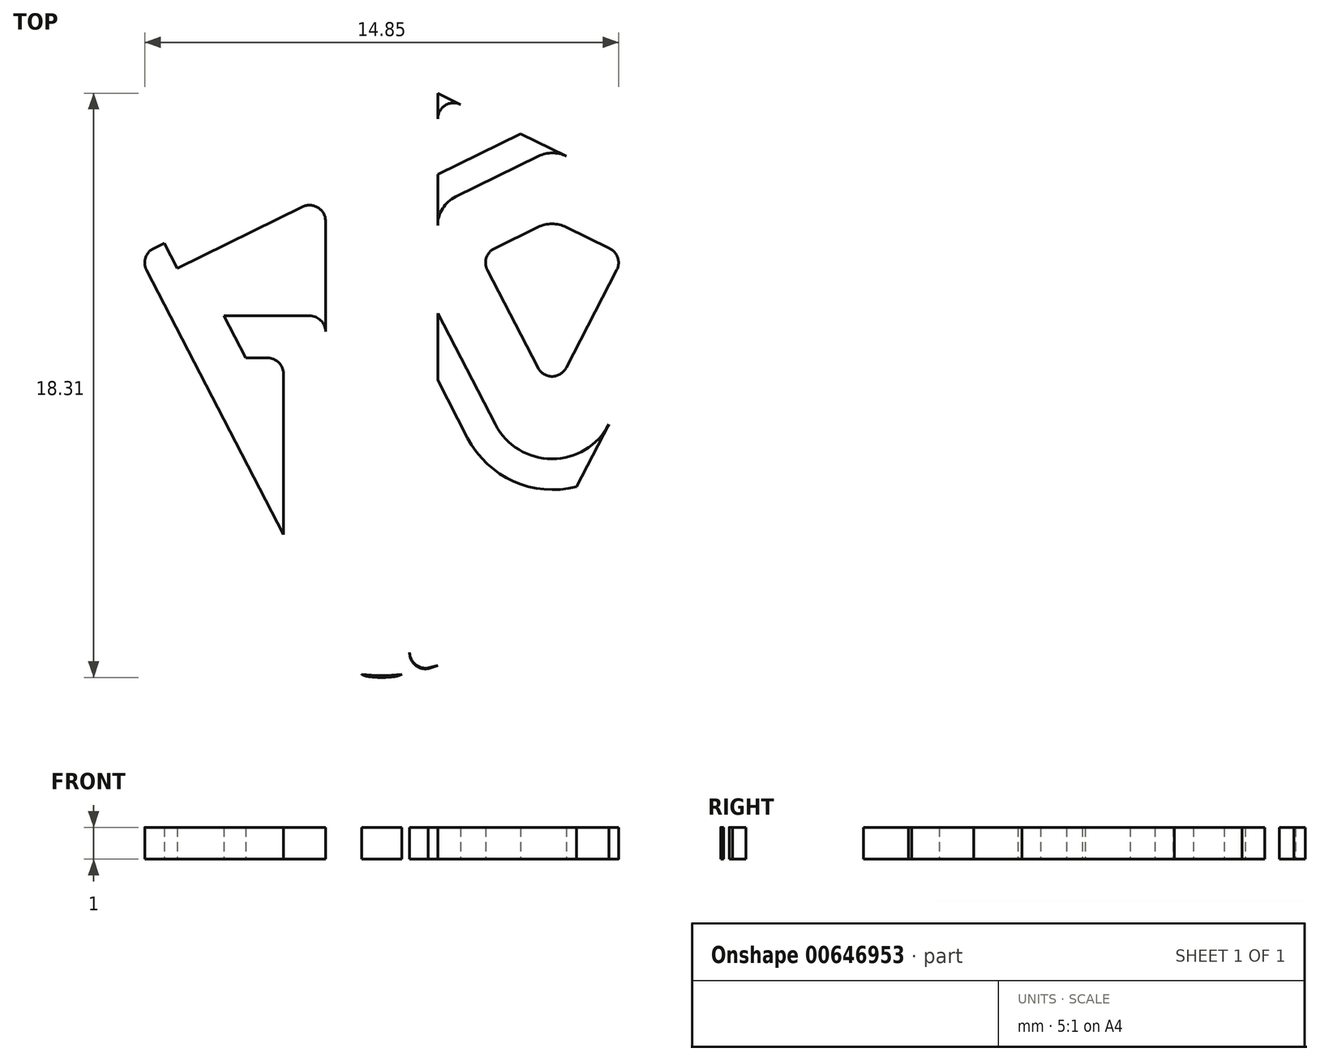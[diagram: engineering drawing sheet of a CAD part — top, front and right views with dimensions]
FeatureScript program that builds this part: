
annotation { "Feature Type Name" : "Feature", "Feature Type Description" : "" }
export const myFeature = defineFeature(function(context is Context, id is Id, definition is map)
    precondition{}
    {
        {
            var Q0;
            Q0=qCreatedBy(makeId("Top.planeOp"),FACE);
            var sketch = newSketch(context, id + "F0", { "sketchPlane" : qUnion([Q0])});
            skArc(sketch, "E0.MirrorCS", {"start": v(-12.62, 8.93) * mm, "mid": v(-12.18, 9.03) * mm, "end": v(-11.74, 8.93) * mm});
            skArc(sketch, "E1.MirrorCS", {"start": v(-1.42, 3.88) * mm, "mid": v(-0.9, 3.3) * mm, "end": v(-0.97, 2.52) * mm});
            skArc(sketch, "E2.MirrorCS", {"start": v(-23.38, 2.52) * mm, "mid": v(-23.45, 3.3) * mm, "end": v(-22.94, 3.88) * mm});
            skPoint(sketch, "E3.MirrorP", {"position": v(-23.85, 3.43) * mm});
            skArc(sketch, "E4.MirrorCS", {"start": v(-6.85, -8.84) * mm, "mid": v(-12.18, -12.09) * mm, "end": v(-17.5, -8.84) * mm});
            skLineSegment(sketch, "E5.MirrorCS", {"start": v(-4.15, -3.64) * mm, "end": v(-0.97, 2.52) * mm});
            skLineSegment(sketch, "E6.MirrorCS", {"start": v(-12.62, 8.93) * mm, "end": v(-22.94, 3.88) * mm});
            skLineSegment(sketch, "E7.MirrorCS", {"start": v(-23.38, 2.52) * mm, "end": v(-17.5, -8.84) * mm});
            skLineSegment(sketch, "E8.MirrorCS", {"start": v(-1.42, 3.88) * mm, "end": v(-11.74, 8.93) * mm});
            skLineSegment(sketch, "E9", {"start": v(-22.26, 2.53) * mm, "end": v(-16.62, -8.38) * mm});
            skArc(sketch, "E10.filletArc", {"start": v(-9.67, -10.41) * mm, "mid": v(-8.56, -9.53) * mm, "end": v(-7.74, -8.38) * mm});
            skLineSegment(sketch, "E11.MirrorCS", {"start": v(-10.42, 3.03) * mm, "end": v(-10.42, 0.52) * mm});
            skLineSegment(sketch, "E12.bottom", {"start": v(-15.25, 0.2) * mm, "end": v(-16.07, 0.2) * mm});
            skLineSegment(sketch, "E12.top", {"start": v(-15.75, -1.12) * mm, "end": v(-16.07, -1.12) * mm});
            skLineSegment(sketch, "E13", {"start": v(-15.25, 0.2) * mm, "end": v(-14.44, 0.2) * mm});
            skPoint(sketch, "E14", {"position": v(-16.57, -8.47) * mm});
            skPoint(sketch, "E15", {"position": v(-15.25, -10.03) * mm});
            skPoint(sketch, "E16", {"position": v(-13.94, -10.77) * mm});
            skPoint(sketch, "E17", {"position": v(-13.06, -11) * mm});
            skPoint(sketch, "E18", {"position": v(-11.3, -11) * mm});
            skPoint(sketch, "E19", {"position": v(-10.42, -10.77) * mm});
            skPoint(sketch, "E20", {"position": v(-9.1, -10.03) * mm});
            skPoint(sketch, "E21", {"position": v(-9.1, -6.67) * mm});
            skPoint(sketch, "E22", {"position": v(-2.78, 1.2) * mm});
            skPoint(sketch, "E23", {"position": v(-4.57, 2.08) * mm});
            skPoint(sketch, "E24", {"position": v(-9.1, 6.52) * mm});
            skPoint(sketch, "E25", {"position": v(-10.42, 7.17) * mm});
            skPoint(sketch, "E26", {"position": v(-11.3, 7.6) * mm});
            skPoint(sketch, "E27", {"position": v(-13.06, 7.6) * mm});
            skPoint(sketch, "E28", {"position": v(-13.94, 7.17) * mm});
            skPoint(sketch, "E29", {"position": v(-15.25, 4.3) * mm});
            skPoint(sketch, "E30", {"position": v(-13.94, 4.94) * mm});
            skPoint(sketch, "E31", {"position": v(-13.06, 5.37) * mm});
            skPoint(sketch, "E32", {"position": v(-10.42, 4.94) * mm});
            skPoint(sketch, "E33", {"position": v(-21.58, 1.2) * mm});
            skPoint(sketch, "E34", {"position": v(-19.78, 2.08) * mm});
            skPoint(sketch, "E35", {"position": v(-16.57, -4.12) * mm});
            skPoint(sketch, "E36", {"position": v(-16.57, -1.12) * mm});
            skPoint(sketch, "E37", {"position": v(-16.57, 0.2) * mm});
            skPoint(sketch, "E38", {"position": v(-15.25, 0.2) * mm});
            skPoint(sketch, "E39", {"position": v(-15.25, -1.12) * mm});
            skPoint(sketch, "E40", {"position": v(-13.94, 0.2) * mm});
            skLineSegment(sketch, "E41", {"start": v(-2.78, 1.2) * mm, "end": v(-2.1, 2.53) * mm});
            skLineSegment(sketch, "E42", {"start": v(-3.82, 3.94) * mm, "end": v(-6.39, 5.2) * mm});
            skLineSegment(sketch, "E43", {"start": v(-6.4, -1.43) * mm, "end": v(-4.8, 1.63) * mm});
            skLineSegment(sketch, "E44", {"start": v(-5.03, 2.3) * mm, "end": v(-6.4, 2.97) * mm});
            skLineSegment(sketch, "E45", {"start": v(-9.1, 3.5) * mm, "end": v(-9.1, -6.67) * mm});
            skLineSegment(sketch, "E46", {"start": v(-22.04, 3.2) * mm, "end": v(-14.65, 6.82) * mm});
            skLineSegment(sketch, "E47", {"start": v(-12.78, 7.74) * mm, "end": v(-12.4, 7.92) * mm});
            skLineSegment(sketch, "E48", {"start": v(-11.96, 7.92) * mm, "end": v(-11.58, 7.74) * mm});
            skLineSegment(sketch, "E49", {"start": v(-15.25, 4.3) * mm, "end": v(-19.32, 2.3) * mm});
            skLineSegment(sketch, "E50", {"start": v(-19.55, 1.63) * mm, "end": v(-16.57, -4.12) * mm});
            skLineSegment(sketch, "E51", {"start": v(-15.25, -1.62) * mm, "end": v(-15.25, -10.03) * mm});
            skPoint(sketch, "E52", {"position": v(-15.25, -6.67) * mm});
            skLineSegment(sketch, "E53", {"start": v(-16.57, -4.12) * mm, "end": v(-15.25, -6.67) * mm});
            skLineSegment(sketch, "E54", {"start": v(-15.25, 4.3) * mm, "end": v(-14.65, 4.59) * mm});
            skLineSegment(sketch, "E55", {"start": v(-9.1, 6.52) * mm, "end": v(-9.7, 6.82) * mm});
            skArc(sketch, "E56.filletArc", {"start": v(-22.04, 3.2) * mm, "mid": v(-22.3, 2.91) * mm, "end": v(-22.26, 2.53) * mm});
            skArc(sketch, "E57.filletArc", {"start": v(-2.1, 2.53) * mm, "mid": v(-2.06, 2.91) * mm, "end": v(-2.32, 3.2) * mm});
            skArc(sketch, "E58.filletArc", {"start": v(-13.94, 6.37) * mm, "mid": v(-14.17, 6.8) * mm, "end": v(-14.65, 6.82) * mm});
            skArc(sketch, "E59.filletArc", {"start": v(-9.7, 6.82) * mm, "mid": v(-10.18, 6.8) * mm, "end": v(-10.42, 6.37) * mm});
            skArc(sketch, "E60.filletArc", {"start": v(-8.38, 3.94) * mm, "mid": v(-8.87, 3.92) * mm, "end": v(-9.1, 3.5) * mm});
            skArc(sketch, "E61.filletArc", {"start": v(-4.8, 1.63) * mm, "mid": v(-4.78, 2.01) * mm, "end": v(-5.03, 2.3) * mm});
            skArc(sketch, "E62.filletArc", {"start": v(-19.32, 2.3) * mm, "mid": v(-19.58, 2.01) * mm, "end": v(-19.55, 1.63) * mm});
            skArc(sketch, "E63.filletArc", {"start": v(-13.94, 4.14) * mm, "mid": v(-14.17, 4.56) * mm, "end": v(-14.65, 4.59) * mm});
            skArc(sketch, "E64.filletArc", {"start": v(-15.25, -1.62) * mm, "mid": v(-15.4, -1.27) * mm, "end": v(-15.75, -1.12) * mm});
            skArc(sketch, "E65.filletArc", {"start": v(-13.94, -0.3) * mm, "mid": v(-14.08, 0.05) * mm, "end": v(-14.44, 0.2) * mm});
            skLineSegment(sketch, "E66", {"start": v(-13.94, 4.14) * mm, "end": v(-13.94, 6.37) * mm});
            skArc(sketch, "E67.filletArc", {"start": v(-11.96, 7.92) * mm, "mid": v(-12.18, 7.97) * mm, "end": v(-12.4, 7.92) * mm});
            skArc(sketch, "E68.filletArc", {"start": v(-12.78, 7.74) * mm, "mid": v(-12.98, 7.55) * mm, "end": v(-13.06, 7.29) * mm});
            skArc(sketch, "E69.filletArc", {"start": v(-11.3, 7.29) * mm, "mid": v(-11.37, 7.55) * mm, "end": v(-11.58, 7.74) * mm});
            skArc(sketch, "E70.filletArc", {"start": v(-10.42, -9.98) * mm, "mid": v(-10.17, -10.41) * mm, "end": v(-9.67, -10.41) * mm});
            skArc(sketch, "E71.MirrorCS", {"start": v(-14.69, -10.41) * mm, "mid": v(-15.8, -9.53) * mm, "end": v(-16.62, -8.38) * mm});
            skArc(sketch, "E72.MirrorCS", {"start": v(-13.94, -9.98) * mm, "mid": v(-14.19, -10.41) * mm, "end": v(-14.69, -10.41) * mm});
            skArc(sketch, "E73", {"start": v(-12.63, -11.1) * mm, "mid": v(-12.18, -11.14) * mm, "end": v(-11.72, -11.1) * mm});
            skLineSegment(sketch, "E74", {"start": v(-13.94, -9.98) * mm, "end": v(-13.94, -0.3) * mm});
            skLineSegment(sketch, "E75", {"start": v(-13.06, -10.37) * mm, "end": v(-13.06, 6.8) * mm});
            skLineSegment(sketch, "E76", {"start": v(-11.3, 7.29) * mm, "end": v(-11.3, -10.35) * mm});
            skArc(sketch, "E77.filletArc", {"start": v(-13.06, -10.61) * mm, "mid": v(-12.94, -10.94) * mm, "end": v(-12.63, -11.1) * mm});
            skArc(sketch, "E78.filletArc", {"start": v(-11.72, -11.1) * mm, "mid": v(-11.42, -10.94) * mm, "end": v(-11.3, -10.61) * mm});
            skLineSegment(sketch, "E79", {"start": v(-16.07, 0.2) * mm, "end": v(-17.12, 0.2) * mm});
            skLineSegment(sketch, "E80", {"start": v(-16.07, -1.12) * mm, "end": v(-16.57, -1.12) * mm});
            skPoint(sketch, "E81", {"position": v(-16.43, -1.12) * mm});
            skLineSegment(sketch, "E82", {"start": v(-16.43, -1.12) * mm, "end": v(-17.12, 0.2) * mm});
            skPoint(sketch, "E83", {"position": v(-6.84, 2.08) * mm});
            skPoint(sketch, "E84", {"position": v(-6.84, 3.19) * mm});
            skPoint(sketch, "E85", {"position": v(-6.84, -2.3) * mm});
            skPoint(sketch, "E86", {"position": v(-9.1, 2.08) * mm});
            skLineSegment(sketch, "E87", {"start": v(-7.28, 2.97) * mm, "end": v(-8.64, 2.3) * mm});
            skLineSegment(sketch, "E88", {"start": v(-8.87, 1.63) * mm, "end": v(-7.28, -1.43) * mm});
            skPoint(sketch, "E89", {"position": v(-6.83, 5.4) * mm});
            skPoint(sketch, "E90", {"position": v(-5.42, 0.45) * mm});
            skPoint(sketch, "E91", {"position": v(-10.42, 3.65) * mm});
            skLineSegment(sketch, "E92", {"start": v(-9.86, 3.93) * mm, "end": v(-7.27, 5.2) * mm});
            skPoint(sketch, "E93", {"position": v(-7.96, -4.47) * mm});
            skPoint(sketch, "E94", {"position": v(-10.42, 0.28) * mm});
            skPoint(sketch, "E95", {"position": v(-9.1, -2.27) * mm});
            skLineSegment(sketch, "E96", {"start": v(-6.84, 3.19) * mm, "end": v(-6.84, 2.08) * mm});
            skPoint(sketch, "E97", {"position": v(-3.26, 0.28) * mm});
            skPoint(sketch, "E98", {"position": v(-3.26, 3.66) * mm});
            skLineSegment(sketch, "E99", {"start": v(-3.26, 3.04) * mm, "end": v(-3.26, 0.52) * mm});
            skLineSegment(sketch, "E100", {"start": v(-12.18, -6.09) * mm, "end": v(-12.18, -8.2) * mm});
            skLineSegment(sketch, "E101.MirrorCS", {"start": v(-21.1, 3.66) * mm, "end": v(-21.1, 0.28) * mm});
            skLineSegment(sketch, "E102.MirrorCS", {"start": v(-4.57, 2.08) * mm, "end": v(-6.84, -2.3) * mm});
            skLineSegment(sketch, "E103.MirrorCS", {"start": v(-6.84, 3.19) * mm, "end": v(-4.57, 2.08) * mm});
            skPoint(sketch, "E104", {"position": v(-11.3, 5.38) * mm});
            skPoint(sketch, "E105", {"position": v(-11.3, -10.04) * mm});
            skPoint(sketch, "E106", {"position": v(-13.06, -10.04) * mm});
            skPoint(sketch, "E107", {"position": v(-12.17, 5.8) * mm});
            skPoint(sketch, "E108", {"position": v(-13.06, -6.65) * mm});
            skPoint(sketch, "E109", {"position": v(-11.3, -6.65) * mm});
            skLineSegment(sketch, "E110", {"start": v(-13.94, 7.17) * mm, "end": v(-13.78, 7.25) * mm});
            skLineSegment(sketch, "E111", {"start": v(-13.06, 5.37) * mm, "end": v(-13.06, 7.6) * mm});
            skArc(sketch, "E112.filletArc", {"start": v(-13.06, 6.8) * mm, "mid": v(-13.3, 7.22) * mm, "end": v(-13.78, 7.25) * mm});
            skLineSegment(sketch, "E113", {"start": v(-13.94, 7.17) * mm, "end": v(-12.78, 7.74) * mm});
            skLineSegment(sketch, "E114", {"start": v(-11.3, -10.04) * mm, "end": v(-11.3, -11) * mm});
            skLineSegment(sketch, "E115", {"start": v(-10.42, -10.77) * mm, "end": v(-10.67, -10.83) * mm});
            skArc(sketch, "E116.filletArc", {"start": v(-11.3, -10.35) * mm, "mid": v(-11.1, -10.75) * mm, "end": v(-10.67, -10.83) * mm});
            skLineSegment(sketch, "E117", {"start": v(-13.06, -10.04) * mm, "end": v(-13.06, -11) * mm});
            skLineSegment(sketch, "E118", {"start": v(-14.06, -10.77) * mm, "end": v(-13.67, -10.86) * mm});
            skPoint(sketch, "E119.newPointA", {"position": v(-13.06, -10.61) * mm});
            skArc(sketch, "E119.filletArc", {"start": v(-13.67, -10.86) * mm, "mid": v(-13.25, -10.77) * mm, "end": v(-13.06, -10.37) * mm});
            skLineSegment(sketch, "E120", {"start": v(-21.58, 1.2) * mm, "end": v(-16.62, -8.38) * mm});
            skPoint(sketch, "E121", {"position": v(-12.18, -16.97) * mm});
            skArc(sketch, "E122.filletArc", {"start": v(-16.62, -8.38) * mm, "mid": v(-12.18, -11.09) * mm, "end": v(-7.74, -8.38) * mm});
            skArc(sketch, "E123.filletArc", {"start": v(-6.39, 5.2) * mm, "mid": v(-6.83, 5.3) * mm, "end": v(-7.27, 5.2) * mm});
            skArc(sketch, "E124.filletArc", {"start": v(-3.26, 3.04) * mm, "mid": v(-3.4, 3.57) * mm, "end": v(-3.82, 3.94) * mm});
            skArc(sketch, "E125.filletArc", {"start": v(-3.37, 0.06) * mm, "mid": v(-3.28, 0.28) * mm, "end": v(-3.26, 0.52) * mm});
            skArc(sketch, "E126.filletArc", {"start": v(-9.86, 3.93) * mm, "mid": v(-10.27, 3.56) * mm, "end": v(-10.42, 3.03) * mm});
            skArc(sketch, "E127.filletArc", {"start": v(-10.42, 0.52) * mm, "mid": v(-10.4, 0.28) * mm, "end": v(-10.3, 0.06) * mm});
            skArc(sketch, "E128.filletArc", {"start": v(-6.4, 2.97) * mm, "mid": v(-6.84, 3.08) * mm, "end": v(-7.28, 2.97) * mm});
            skArc(sketch, "E129.filletArc", {"start": v(-8.64, 2.3) * mm, "mid": v(-8.9, 2.01) * mm, "end": v(-8.87, 1.63) * mm});
            skLineSegment(sketch, "E130", {"start": v(-3.82, 3.94) * mm, "end": v(-11.3, 7.6) * mm});
            skLineSegment(sketch, "E131", {"start": v(-10.42, 0.52) * mm, "end": v(-10.42, 7.17) * mm});
            skLineSegment(sketch, "E132", {"start": v(-9.77, 4.95) * mm, "end": v(-7.83, 5.9) * mm});
            skLineSegment(sketch, "E133", {"start": v(-7.83, 5.9) * mm, "end": v(-9.77, 4.95) * mm});
            skLineSegment(sketch, "E134", {"start": v(-9.77, 4.95) * mm, "end": v(-10.42, 4.63) * mm});
            skPoint(sketch, "E135", {"position": v(-8.5, -3.42) * mm});
            skLineSegment(sketch, "E136", {"start": v(-16.9, 2.51) * mm, "end": v(-19.8, 1.1) * mm});
            skLineSegment(sketch, "E137", {"start": v(-19.8, 1.1) * mm, "end": v(-16.9, 2.51) * mm});
            skLineSegment(sketch, "E138", {"start": v(-16.9, 2.51) * mm, "end": v(-14.65, 3.61) * mm});
            skLineSegment(sketch, "E139", {"start": v(-19.12, 0.8) * mm, "end": v(-18.34, 1.21) * mm});
            skLineSegment(sketch, "E140", {"start": v(-18.34, 1.21) * mm, "end": v(-19.55, 3.55) * mm});
            skLineSegment(sketch, "E141", {"start": v(-19.55, 3.55) * mm, "end": v(-18.34, 1.21) * mm});
            skLineSegment(sketch, "E142", {"start": v(-19.55, 3.55) * mm, "end": v(-15.64, -4.01) * mm});
            skLineSegment(sketch, "E143", {"start": v(-16.13, -2.63) * mm, "end": v(-16.13, -3.81) * mm});
            skLineSegment(sketch, "E144", {"start": v(-16.13, -1.46) * mm, "end": v(-16.13, -3.81) * mm});
            skLineSegment(sketch, "E145", {"start": v(-13.94, 3.16) * mm, "end": v(-13.94, -0.3) * mm});
            skLineSegment(sketch, "E146", {"start": v(-15.25, 1.07) * mm, "end": v(-18.6, 1.07) * mm});
            skLineSegment(sketch, "E147", {"start": v(-18.6, 1.07) * mm, "end": v(-15.25, 1.07) * mm});
            skLineSegment(sketch, "E148", {"start": v(-13.7, 1.07) * mm, "end": v(-15.25, 1.07) * mm});
            skArc(sketch, "E149.filletArc", {"start": v(-13.94, 3.16) * mm, "mid": v(-14.17, 3.59) * mm, "end": v(-14.65, 3.61) * mm});
            skLineSegment(sketch, "E150", {"start": v(-2.38, 2.4) * mm, "end": v(-2.38, 1.75) * mm});
            skLineSegment(sketch, "E151", {"start": v(-2.38, 1.75) * mm, "end": v(-2.38, 3.6) * mm});
            skLineSegment(sketch, "E152", {"start": v(-3.82, 3.94) * mm, "end": v(-1.86, 2.98) * mm});
            skLineSegment(sketch, "E153", {"start": v(-16.07, -2) * mm, "end": v(-17.03, -2) * mm});
            skArc(sketch, "E154.filletArc", {"start": v(-7.28, -1.43) * mm, "mid": v(-6.84, -1.7) * mm, "end": v(-6.4, -1.43) * mm});
            skLineSegment(sketch, "E155", {"start": v(-7.74, -8.38) * mm, "end": v(-6.84, -6.65) * mm});
            skPoint(sketch, "E156", {"position": v(-7.9, 1.68) * mm});
            skPoint(sketch, "E157", {"position": v(-6.86, 2.22) * mm});
            skPoint(sketch, "E158", {"position": v(-5.77, 1.69) * mm});
            skPoint(sketch, "E159", {"position": v(-6.84, -0.38) * mm});
            skLineSegment(sketch, "E160", {"start": v(-7.9, 1.68) * mm, "end": v(-6.86, 2.22) * mm});
            skLineSegment(sketch, "E161", {"start": v(-6.86, 2.22) * mm, "end": v(-5.77, 1.69) * mm});
            skLineSegment(sketch, "E162", {"start": v(-5.77, 1.69) * mm, "end": v(-6.84, -0.38) * mm});
            skLineSegment(sketch, "E163", {"start": v(-6.84, -0.38) * mm, "end": v(-7.9, 1.68) * mm});
            skLineSegment(sketch, "E164.MirrorCS", {"start": v(-10.42, -9.98) * mm, "end": v(-10.42, -0.3) * mm});
            skPoint(sketch, "E165", {"position": v(-6.82, -8.79) * mm});
            skLineSegment(sketch, "E166", {"start": v(-6.85, -8.84) * mm, "end": v(-6.82, -8.79) * mm});
            skPoint(sketch, "E167", {"position": v(-6.84, -6.65) * mm});
            skLineSegment(sketch, "E168", {"start": v(-2.78, 1.2) * mm, "end": v(-5.06, -3.21) * mm});
            skLineSegment(sketch, "E169", {"start": v(-8.61, -3.21) * mm, "end": v(-10.42, 0.28) * mm});
            skLineSegment(sketch, "E170", {"start": v(-10.42, 0.52) * mm, "end": v(-10.42, -0.3) * mm});
            skArc(sketch, "E171.filletArc", {"start": v(-8.61, -3.21) * mm, "mid": v(-6.84, -4.3) * mm, "end": v(-5.06, -3.21) * mm});
            skPoint(sketch, "E172", {"position": v(-10.42, -1.83) * mm});
            skPoint(sketch, "E173", {"position": v(-9.1, -4.38) * mm});
            skLineSegment(sketch, "E174", {"start": v(-5.5, -4.07) * mm, "end": v(-5.06, -3.21) * mm});
            skLineSegment(sketch, "E175", {"start": v(-9.1, -2.27) * mm, "end": v(-8.17, -4.07) * mm});
            skPoint(sketch, "E176", {"position": v(-0.97, 2.52) * mm});
            skPoint(sketch, "E177", {"position": v(-4.15, -3.64) * mm});
            skLineSegment(sketch, "E178", {"start": v(-10.42, -1.83) * mm, "end": v(-9.48, -3.64) * mm});
            skArc(sketch, "E179.filletArc", {"start": v(-9.48, -3.64) * mm, "mid": v(-6.82, -5.26) * mm, "end": v(-4.15, -3.64) * mm});
            skLineSegment(sketch, "E180", {"start": v(-6.82, -8.79) * mm, "end": v(-4.15, -3.64) * mm});
            skLineSegment(sketch, "E181", {"start": v(-6.84, -6.65) * mm, "end": v(-3.26, 0.28) * mm});
            skArc(sketch, "E182.MirrorCS", {"start": v(-10.68, -10.86) * mm, "mid": v(-11.1, -10.77) * mm, "end": v(-11.3, -10.37) * mm});
            skArc(sketch, "E183.MirrorCS", {"start": v(-11.3, -10.61) * mm, "mid": v(-11.42, -10.94) * mm, "end": v(-11.72, -11.1) * mm});
            skArc(sketch, "E184.MirrorCS", {"start": v(-7.74, -8.38) * mm, "mid": v(-12.18, -11.09) * mm, "end": v(-16.62, -8.38) * mm});
            skSolve(sketch);
        }
        {
            var Q0;
            {var subQ4=sQuery(id+"F0.wireOp",EDGE,"E138");Q0=makeQuery(id+"F0.imprint","IMPRINT",FACE,{"disambiguationData":[TD([[makeQuery(id+"F0.imprint","IMPRINT",EDGE,{"derivedFrom":subQ4}),-1.0]])]});}
            var Q1;
            Q1=makeQuery(id+"F0.imprint","IMPRINT",FACE,{"disambiguationData":[TD([[makeQuery(id+"F0.imprint","IMPRINT",EDGE,{"derivedFrom":sQuery(id+"F0.wireOp",EDGE,"E12.bottom")}),-1.0]])]});
            var Q2;
            {var subQ0=sQuery(id+"F0.wireOp",EDGE,"E144");var subQ5=makeQuery(id+"F0.imprint","IMPRINT",VERTEX,{"derivedFrom":subQ0});Q2=makeQuery(id+"F0.imprint","IMPRINT",FACE,{"disambiguationData":[TD([[makeQuery(id+"F0.imprint","IMPRINT",EDGE,{"disambiguationData":[TD([[subQ5,1.0]])],"derivedFrom":subQ0}),-1.0]])]});}
            var Q3;
            {var subQ0=sQuery(id+"F0.wireOp",EDGE,"E62.filletArc");Q3=makeQuery(id+"F0.imprint","IMPRINT",FACE,{"disambiguationData":[TD([[makeQuery(id+"F0.imprint","IMPRINT",EDGE,{"derivedFrom":subQ0}),1.0]])]});}
            var Q4;
            {var subQ1=sQuery(id+"F0.wireOp",EDGE,"E139");var subQ4=sQuery(id+"F0.wireOp",EDGE,"E50");var subQ5=makeQuery(id+"F0.imprint","INTERSECT",VERTEX,{"derivedFrom":[subQ4,subQ1]});Q4=makeQuery(id+"F0.imprint","IMPRINT",FACE,{"disambiguationData":[TD([[makeQuery(id+"F0.imprint","IMPRINT",EDGE,{"disambiguationData":[TD([[subQ5,1.0]])],"derivedFrom":subQ4}),1.0]])]});}
            var Q5;
            {var subQ0=sQuery(id+"F0.wireOp",EDGE,"E142");var subQ1=sQuery(id+"F0.wireOp",EDGE,"E139");var subQ2=makeQuery(id+"F0.imprint","INTERSECT",VERTEX,{"derivedFrom":[subQ1,subQ0]});Q5=makeQuery(id+"F0.imprint","IMPRINT",FACE,{"disambiguationData":[TD([[makeQuery(id+"F0.imprint","IMPRINT",EDGE,{"disambiguationData":[TD([[subQ2,1.0]])],"derivedFrom":subQ1}),-1.0]])]});}
            var Q6;
            {var subQ0=sQuery(id+"F0.wireOp",EDGE,"ozTpNQaU-grU3-HA9w-UyX2-o1CqBorec6r5");Q6=makeQuery(id+"F0.imprint","IMPRINT",FACE,{"disambiguationData":[TD([[makeQuery(id+"F0.imprint","IMPRINT",EDGE,{"derivedFrom":subQ0}),-1.0]])]});}
            var Q7;
            {var subQ2=sQuery(id+"F0.wireOp",EDGE,"3e2ccfe4-6b2a-43d4-8b51-7597902346a8.filletArc");Q7=makeQuery(id+"F0.imprint","IMPRINT",FACE,{"disambiguationData":[TD([[makeQuery(id+"F0.imprint","IMPRINT",EDGE,{"derivedFrom":subQ2}),-1.0]])]});}
            var Q8;
            Q8=makeQuery(id+"F0.imprint","IMPRINT",FACE,{"disambiguationData":[TD([[makeQuery(id+"F0.imprint","IMPRINT",EDGE,{"derivedFrom":sQuery(id+"F0.wireOp",EDGE,"E92")}),1.0]])]});
            var Q9;
            {var subQ3=sQuery(id+"F0.wireOp",EDGE,"E160");Q9=makeQuery(id+"F0.imprint","IMPRINT",FACE,{"disambiguationData":[TD([[makeQuery(id+"F0.imprint","IMPRINT",EDGE,{"derivedFrom":subQ3}),-1.0]])]});}
            var Q10;
            {var subQ7=sQuery(id+"F0.wireOp",EDGE,"E61.filletArc");Q10=makeQuery(id+"F0.imprint","IMPRINT",FACE,{"disambiguationData":[TD([[makeQuery(id+"F0.imprint","IMPRINT",EDGE,{"derivedFrom":subQ7}),1.0]])]});}
            var Q11;
            {var subQ5=sQuery(id+"F0.wireOp",EDGE,"E171.filletArc");Q11=makeQuery(id+"F0.imprint","IMPRINT",FACE,{"disambiguationData":[TD([[makeQuery(id+"F0.imprint","IMPRINT",EDGE,{"derivedFrom":subQ5}),-1.0]])]});}
            var Q12;
            {var subQ8=sQuery(id+"F0.wireOp",EDGE,"Ewz0VHGi-sKfj-zBBT-7Waf-a84nxzi6t6Pn");Q12=makeQuery(id+"F0.imprint","IMPRINT",FACE,{"disambiguationData":[TD([[makeQuery(id+"F0.imprint","IMPRINT",EDGE,{"derivedFrom":subQ8}),1.0]])]});}
            var Q13;
            {var subQ8=sQuery(id+"F0.wireOp",EDGE,"E178");Q13=makeQuery(id+"F0.imprint","IMPRINT",FACE,{"disambiguationData":[TD([[makeQuery(id+"F0.imprint","IMPRINT",EDGE,{"derivedFrom":subQ8}),1.0]])]});}
            var Q14;
            {var subQ0=sQuery(id+"F0.wireOp",EDGE,"E59.filletArc");Q14=makeQuery(id+"F0.imprint","IMPRINT",FACE,{"disambiguationData":[TD([[makeQuery(id+"F0.imprint","IMPRINT",EDGE,{"derivedFrom":subQ0}),-1.0]])]});}
            var Q15;
            {var subQ2=sQuery(id+"F0.wireOp",EDGE,"E115");Q15=makeQuery(id+"F0.imprint","IMPRINT",FACE,{"disambiguationData":[TD([[makeQuery(id+"F0.imprint","IMPRINT",EDGE,{"derivedFrom":subQ2}),1.0]])]});}
            var Q16;
            {var subQ0=sQuery(id+"F0.wireOp",EDGE,"E73");Q16=makeQuery(id+"F0.imprint","IMPRINT",FACE,{"disambiguationData":[TD([[makeQuery(id+"F0.imprint","IMPRINT",EDGE,{"derivedFrom":subQ0}),1.0]])]});}
            var Q17;
            Q17=makeQuery(id+"F0.imprint","IMPRINT",FACE,{"disambiguationData":[TD([[makeQuery(id+"F0.imprint","IMPRINT",EDGE,{"derivedFrom":sQuery(id+"F0.wireOp",EDGE,"E0.MirrorCS")}),-1.0]])]});
            extrude(context, id + "F1", {"entities" : qUnion([Q0, Q1, Q2, Q3, Q4, Q5, Q6, Q7, Q8, Q9, Q10, Q11, Q12, Q13, Q14, Q15, Q16, Q17]), "depth" : 1 * mm, "offsetDistance" : 25 * mm});
        }
    });
